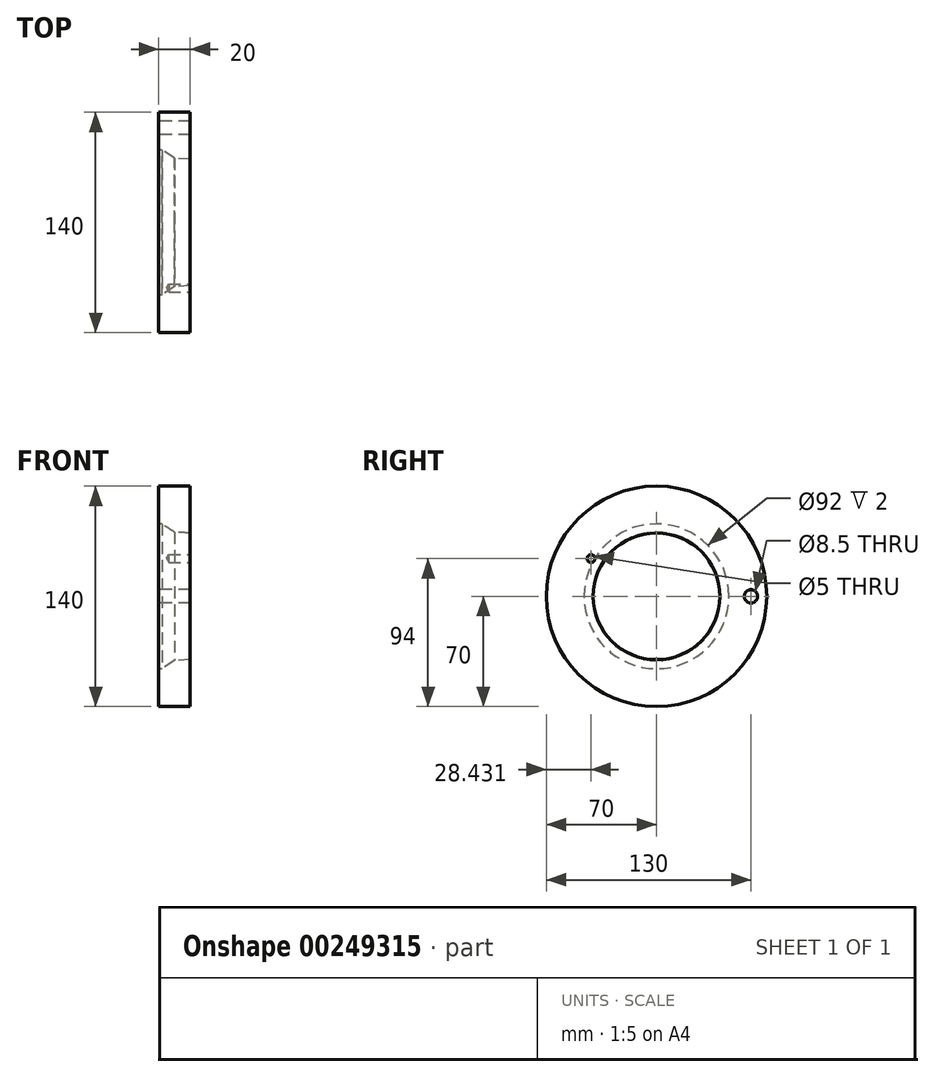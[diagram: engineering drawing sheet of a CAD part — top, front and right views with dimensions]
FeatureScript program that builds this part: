
annotation { "Feature Type Name" : "Feature", "Feature Type Description" : "" }
export const myFeature = defineFeature(function(context is Context, id is Id, definition is map)
    precondition{}
    {
        {
            var Q0;
            Q0=qCreatedBy(makeId("Front.planeOp"),FACE);
            var sketch = newSketch(context, id + "F0", { "sketchPlane" : qUnion([Q0])});
            skLineSegment(sketch, "E0", {"start": v(0, 40.2) * mm, "end": v(0, 70) * mm});
            skLineSegment(sketch, "E1", {"start": v(0, 70) * mm, "end": v(-20, 70) * mm});
            skLineSegment(sketch, "E2", {"start": v(0, 0) * mm, "end": v(24.78, 0) * mm});
            skLineSegment(sketch, "E3", {"start": v(-20, 46) * mm, "end": v(-20, 70) * mm});
            skLineSegment(sketch, "E4", {"start": v(0, 40.2) * mm, "end": v(-10, 40.81) * mm});
            skLineSegment(sketch, "E5", {"start": v(-18, 46) * mm, "end": v(-10, 40.81) * mm});
            skLineSegment(sketch, "E6", {"start": v(-18, 46) * mm, "end": v(-20, 46) * mm});
            skSolve(sketch);
        }
        {
            var Q0;
            Q0=makeQuery(id+"F0.imprint","IMPRINT",FACE,{"disambiguationData":[TD([[makeQuery(id+"F0.imprint","IMPRINT",EDGE,{"derivedFrom":sQuery(id+"F0.wireOp",EDGE,"E0")}),1.0]])]});
            var Q1;
            Q1=sQuery(id+"F0.wireOp",EDGE,"E2");
            revolve(context, id + "F1", {"entities" : qUnion([Q0]), "axis" : qUnion([Q1]), "revolveType" : RevolveType.FULL});
        }
        {
            var Q0;
            Q0=makeQuery(id+"F1.opRevolve","SWEPT_FACE",FACE,{"disambiguationData":[OSD([sQuery(id+"F0.wireOp",EDGE,"E3")])]});
            var sketch = newSketch(context, id + "F2", { "sketchPlane" : qUnion([Q0])});
            skCircle(sketch, "E7", {"center": v(-60, 0) * mm, "radius": 4.25 * mm});
            skSolve(sketch);
        }
        {
            var Q0;
            Q0=makeQuery(id+"F2.imprint","IMPRINT",FACE,{"disambiguationData":[TD([[makeQuery(id+"F2.imprint","IMPRINT",EDGE,{"derivedFrom":sQuery(id+"F2.wireOp",EDGE,"E7")}),1.0]])]});
            extrude(context, id + "F3", {"entities" : qUnion([Q0]), "operationType" : NewBodyOperationType.REMOVE, "endBound" : BoundingType.THROUGH_ALL, "oppositeDirection" : true, "depth" : 25 * mm, "offsetDistance" : 25 * mm});
        }
        {
            var Q0;
            Q0=makeQuery(id+"F1.opRevolve","SWEPT_FACE",FACE,{"disambiguationData":[OSD([sQuery(id+"F0.wireOp",EDGE,"E0")])]});
            var sketch = newSketch(context, id + "F4", { "sketchPlane" : qUnion([Q0])});
            skLineSegment(sketch, "E8", {"start": v(0, 0) * mm, "end": v(-41.57, 24) * mm});
            skCircle(sketch, "E9", {"center": v(-41.57, 24) * mm, "radius": 2.5 * mm});
            skSolve(sketch);
        }
        {
            var Q0;
            Q0=makeQuery(id+"F4.imprint","IMPRINT",FACE,{"disambiguationData":[TD([[makeQuery(id+"F4.imprint","IMPRINT",EDGE,{"derivedFrom":sQuery(id+"F4.wireOp",EDGE,"E9")}),1.0]])]});
            extrude(context, id + "F5", {"entities" : qUnion([Q0]), "operationType" : NewBodyOperationType.REMOVE, "oppositeDirection" : true, "depth" : 15 * mm, "offsetDistance" : 25 * mm});
        }
        {
            var Q0;
            Q0=makeQuery(id+"F5.boolean.opBoolean","COPY",EDGE,{"derivedFrom":makeQuery(id+"F5.opExtrude","CAP_EDGE",EDGE,{"disambiguationData":[OSD([sQuery(id+"F4.wireOp",EDGE,"E9")])],"isStart":false})});
            chamfer(context, id + "F6", {"entities" : qUnion([Q0]), "chamferType" : ChamferType.OFFSET_ANGLE, "width" : 2.5 * mm, "oppositeDirection" : false, "angle" : 31 * degree, "tangentPropagation" : true});
        }
    });
